# Revit family: Shower-Showerhead-KOHLER-Awaken-K-72419
name_source: partatom
category: Plumbing Fixtures
revit_build: Autodesk Revit 2015 (Build: 20140606_1530(x64)
units: mm (PartAtom-declared; Revit-internal decimal feet)

## types (3) — shared parameters
ADA Compliant = Yes
Assembly Code = D2010700
CW Connection = Yes
Date Modified = 09/18/2017
Default Elevation = 0"
Description = G110 2.0 gpm multifunction showerhead
Flow Rate = 2 GPM
HW Connection = No
Height = 2 7/8"
Inlet Connection = Inlet Connection
Length = 4 5/16"
Manufacturer = Kohler
MasterFormat 1995 = 15410
MasterFormat 2004 = 22.41.39
Material = Kohler Material
Outlet Connection = Outlet Connection
Pressure = 0.00 psi
Product Documentation Link = http://www.us.kohler.com
Product Name = Awaken
Product Page URL = http://www.us.kohler.com
URL = http://www.us.kohler.com
Width = 4 19/32"

## per-type parameters (varying)
| type | Finish | Model | Type |
| CP-Polished Chrome | Metal-Kohler-CP-Polished Chrome | K-72419-CP | 1 |
| BN-Vibrant Brushed Nickel | Metal-Kohler-BN-Vibrant Brushed Nickel | K-72419-BN | 2 |
| 2BZ-Oil Rubbed Bronze | Metal-Kohler-2BZ-Oil Rubbed Bronze | K-72419-2BZ | 3 |

## geometry (parser evidence)
native form markers: Blend x4, Sweep x5
no freeform markers — native parametric forms only
